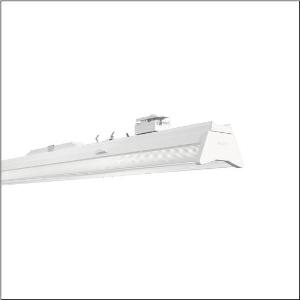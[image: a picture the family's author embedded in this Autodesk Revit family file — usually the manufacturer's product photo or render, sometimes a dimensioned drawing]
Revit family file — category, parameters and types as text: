
# Revit family: licross_r__11_performance_ho_51tm16mn4gxm_a288
name_source: partatom
category: Lighting Fixtures
units: mm (PartAtom-declared; Revit-internal decimal feet)

## family parameters
Cut with Voids When Loaded = No
Host = Face
Light Source = No
Part Type = Normal
Room Calculation Point = No
Round Connector Dimension = Use Diameter
Shared = No

## types (1)
- --- (1 x LED, 16020 lm, 87.4 W, 4000K)
    Apparent Load = 87 VA
    CIE Flux Codes = 63 87 95 78 100
    Color Rendering = 80
    Color Temperature = 4000K
    Default Elevation = 1800 mm
    Description = Licross® 11 Performance HO, luminaire insert, of sheet steel, galvanised, coil coated, white, length: 1.500mm, width: 120mm, height: 123mm, LED rated luminous flux: 16.020lm, light colour: 840, control gear: ON/OFF Multilumen, with plug, 3-pole, with phase selection, mains connection: 220..240V, AC, 50/60Hz, rated input power: 87W, halogen-free wiring, primary light control with lens, of plastic, primary optical cover: cover, of PMMA, light emission: direct/indirect distribution, primary light characteristic: symmetric, protection rating (complete): IP40, insulation class (complete): insulation class I (protective earthing), certification: CE, ENEC, VDE, UKCA, protection symbol: D if used in an environment without relevant dust loads with corresponding accessories, impact resistance: IK06, permissible ambient temperature for indoor applications: -35..+35°C, corresponds to IFS (International Featured Standards) requirements for safety and quality in the food industry, reducing of maximum allowable ambient temperature of 5°C with ceiling mounting, LABS conformity tested according to VDMA 24364:2018-05, packaging unit: 1 piece
    Height = 114 mm
    Lamp = 1 x LED
    Lamp Light Flux = 16020 lm
    Lamp Power = 87.4 W
    Lamp count = 1
    Length = 1500 mm
    Luminous efficacy = 183 lm/W
    Manufacturer = Siteco
    ModVariant = No
    Model = 51TM16MN4GXM
    Mounting Place = Ceiling
    Mounting Type = Pendant
    Number of Poles = 1
    OnlyDefault = Yes
    Power Factor = 1
    Product Name = Licross® 11 Performance HO
    Product group = luminaire insert
    ProductGroupID = 901
    Protection Class = Protection class I
    Protection Degree = IP 40
    RLX_Detail_Level = 1
    RLX_Emergency_Light_Flux = 0 lm
    RLX_Emergency_Type = 0
    RLX_Emergency_Type_DB = No
    RlxData = <blob elided: 31769 chars, md5=38921a98>
    Socket = socket
    Standby Power = 0 W
    System Light Flux = 16020 lm
    System Power = 87 W
    Type Comments = factory setting: luminous flux: 100 % | (A | C | E) | 203 mA
    Type Image = l_1256138.jpg
    URL = http://relux.com
    VarID = @adj_038387
    Voltage = 0 V
    Weight = 0.00 kg
    Width = 120 mm

## geometry (parser evidence)
native form markers: Blend x4, Sweep x10
no freeform markers — native parametric forms only
